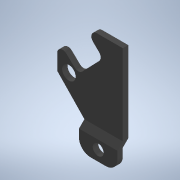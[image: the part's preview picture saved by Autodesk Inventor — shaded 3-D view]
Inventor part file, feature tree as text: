
AUTODESK INVENTOR PART (.ipt)
format: ipt  version: 2022 (Build 260153000, 153)  size: 273,408 bytes
history: native  units: mm
features: extrude x6, sketch x6, fillet x3, chamfer x2, projected_geometry x2, mirror x1
ambient origin geometry x8: Origin, YZ Plane, XZ Plane, XY Plane, X Axis, Y Axis, Z Axis, Center Point
bodies: Solid1 (feature_tree)
feature tree (20):
  extrude  "Extrusion1"  TaperAngle=0.0deg  [1 undecoded]
  extrude  "Extrusion5"  Depth=5.0mm
  fillet  "Fillet2"  Radius=2.5mm
  extrude  "Extrusion6"  Depth=1.0mm
  chamfer  "Chamfer1"  Distance=0.1mm
  extrude  "Extrusion7"  Depth=1.0mm
  chamfer  "Chamfer2"  [1 undecoded]
  extrude  "Extrusion8"  Depth=1.0mm
  extrude  "Extrusion9"  Depth=2.0mm
  fillet  "Fillet3"  Radius=3.525mm
  fillet  "Fillet4"  Radius=2.6mm
  mirror  "Mirror2"
  sketch  "Sketch1"  dims[d6=1.0mm d7=0.0mm]
  sketch  "Sketch7"  dims[d26=4.95mm d27=7.25mm d28=2.5mm d29=4.9mm d30=14.9mm d31=5.1mm d32=5.1mm d33=90.0deg d34=135.0deg d36=0.0mm d37=0.0mm]
  projected_geometry  "Projected Loop2"
  sketch  "Sketch8"  dims[d38=2.5mm d39=5.0mm d40=2.5mm]
  sketch  "Sketch9"  dims[d41=1.0mm d42=7.5mm]
  projected_geometry  "Projected Loop3"
  sketch  "Sketch10"  dims[d43=0.15mm]
  sketch  "Sketch11"  dims[d44=0.15mm d54=0.1mm d55=0.1mm d56=0.0mm d57=4.5mm d58=2.0mm d59=3.525mm d60=2.6mm d61=2.0mm d62=0.0mm d63=5.0mm d64=45.0deg d65=5.0mm d66=45.0deg d67=2.1mm d68=0.2mm d69=0.1mm d70=10.0mm d71=0.0mm d72=1.0mm d73=2.0mm d74=45.0deg d75=1.0mm d76=0.0mm d77=1.0mm d78=2.0mm d79=45.0deg d80=3.8mm d81=1.0mm d82=0.0mm d83=7.0mm d85=6.5mm d86=3.5mm d87=1.0mm d88=0.0mm d89=6.5mm d90=1.0mm d91=1.0mm d5=0.5mm d8=0.872665mm d11=0.5mm d12=0.872665mm d13=0.5mm d14=0.872665mm d25=0.5mm]
note: 2 required parameter values undecoded (feature->parameter linkage not recoverable at this tier; creation-order binding heuristic only, values carry confidence <= 0.55)
